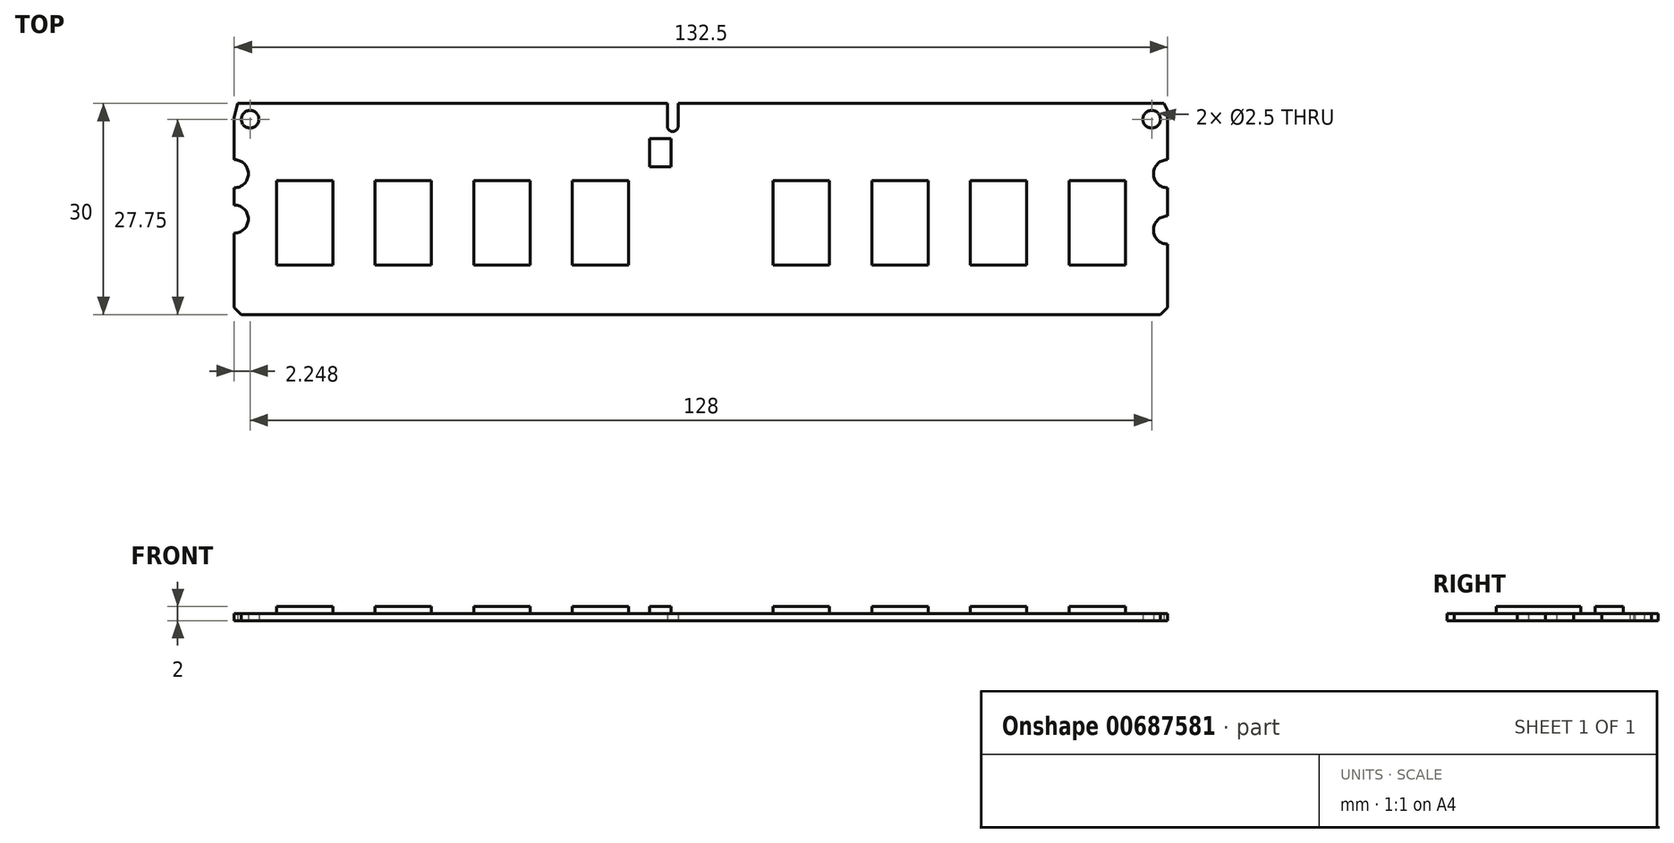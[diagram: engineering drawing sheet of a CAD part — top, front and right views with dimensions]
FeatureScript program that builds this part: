
annotation { "Feature Type Name" : "Feature", "Feature Type Description" : "" }
export const myFeature = defineFeature(function(context is Context, id is Id, definition is map)
    precondition{}
    {
        {
            var Q0;
            Q0=qCreatedBy(makeId("Top.planeOp"),FACE);
            var sketch = newSketch(context, id + "F0", { "sketchPlane" : qUnion([Q0])});
            skLineSegment(sketch, "E0.bottom", {"start": v(-59.31, 12) * mm, "end": v(1.69, 12) * mm});
            skLineSegment(sketch, "E0.top", {"start": v(-58.81, -18) * mm, "end": v(71.69, -18) * mm});
            skLineSegment(sketch, "E0.left", {"start": v(-59.81, 10) * mm, "end": v(-59.81, 4) * mm});
            skLineSegment(sketch, "E0.right", {"start": v(72.69, 11) * mm, "end": v(72.69, 4) * mm});
            skArc(sketch, "E1", {"start": v(72.69, 4) * mm, "mid": v(70.69, 2) * mm, "end": v(72.69, 0) * mm});
            skLineSegment(sketch, "E2", {"start": v(72.69, -17) * mm, "end": v(72.69, -8) * mm});
            skArc(sketch, "E3", {"start": v(72.69, -4) * mm, "mid": v(70.69, -6) * mm, "end": v(72.69, -8) * mm});
            skLineSegment(sketch, "E4.trimOffspring", {"start": v(72.69, -8) * mm, "end": v(72.69, -17) * mm});
            skLineSegment(sketch, "E5.trimOffspring", {"start": v(72.69, 0) * mm, "end": v(72.69, -4) * mm});
            skLineSegment(sketch, "E6", {"start": v(-59.81, -17) * mm, "end": v(-59.81, -6.44) * mm});
            skArc(sketch, "E7", {"start": v(-59.81, 0) * mm, "mid": v(-57.81, 2) * mm, "end": v(-59.81, 4) * mm});
            skArc(sketch, "E8", {"start": v(-59.81, -6.44) * mm, "mid": v(-57.81, -4.44) * mm, "end": v(-59.81, -2.44) * mm});
            skLineSegment(sketch, "E9.trimOffspring", {"start": v(-59.81, -6.44) * mm, "end": v(-59.81, -17) * mm});
            skLineSegment(sketch, "E10.trimOffspring", {"start": v(-59.81, 0) * mm, "end": v(-59.81, -2.44) * mm});
            skLineSegment(sketch, "E11", {"start": v(-59.81, 10) * mm, "end": v(-59.31, 12) * mm});
            skPoint(sketch, "E12.orphan", {"position": v(-59.81, 12) * mm});
            skPoint(sketch, "E13.start.orphan", {"position": v(73.14, 10.06) * mm});
            skLineSegment(sketch, "E14", {"start": v(72.19, 12) * mm, "end": v(72.69, 11) * mm});
            skPoint(sketch, "E15.orphan", {"position": v(72.69, 12) * mm});
            skLineSegment(sketch, "E16", {"start": v(72.69, -17) * mm, "end": v(71.69, -18) * mm});
            skPoint(sketch, "E17.orphan", {"position": v(72.69, -18) * mm});
            skLineSegment(sketch, "E18", {"start": v(-59.81, -17) * mm, "end": v(-58.81, -18) * mm});
            skPoint(sketch, "E19.orphan", {"position": v(-59.81, -18) * mm});
            skLineSegment(sketch, "E20", {"start": v(1.69, 12) * mm, "end": v(1.69, 8.65) * mm});
            skPoint(sketch, "E21.end.orphan", {"position": v(3.19, 12) * mm});
            skLineSegment(sketch, "E22", {"start": v(3.19, 12) * mm, "end": v(3.19, 8.65) * mm});
            skArc(sketch, "E23", {"start": v(1.69, 8.65) * mm, "mid": v(2.44, 8) * mm, "end": v(3.19, 8.65) * mm});
            skPoint(sketch, "E24.orphan", {"position": v(1.69, 8) * mm});
            skLineSegment(sketch, "E25.trimOffspring", {"start": v(3.19, 12) * mm, "end": v(72.19, 12) * mm});
            skPoint(sketch, "E26.end.orphan", {"position": v(3.19, 8) * mm});
            skPoint(sketch, "E26.start.orphan", {"position": v(2.44, 8) * mm});
            skCircle(sketch, "E27", {"center": v(70.44, 9.75) * mm, "radius": 1.25 * mm});
            skPoint(sketch, "E28.end.orphan", {"position": v(70.44, 11) * mm});
            skPoint(sketch, "E29.end.orphan", {"position": v(71.69, 9.75) * mm});
            skCircle(sketch, "E30", {"center": v(-57.56, 9.75) * mm, "radius": 1.25 * mm});
            skPoint(sketch, "E31.end.orphan", {"position": v(-57.56, 11) * mm});
            skPoint(sketch, "E32.end.orphan", {"position": v(-58.81, 9.75) * mm});
            skSolve(sketch);
        }
        {
            var Q0;
            Q0 = qSketchRegion(id + "F0", true);
            extrude(context, id + "F1", {"entities" : qUnion([Q0]), "depth" : 1 * mm, "offsetDistance" : 25 * mm});
        }
        {
            var Q0;
            Q0=makeQuery(id+"F1.opExtrude","CAP_FACE",FACE,{"disambiguationData":[OSD([sQuery(id+"F0.wireOp",EDGE,"E0.bottom"),sQuery(id+"F0.wireOp",EDGE,"E0.top"),sQuery(id+"F0.wireOp",EDGE,"E0.right"),sQuery(id+"F0.wireOp",EDGE,"E1"),sQuery(id+"F0.wireOp",EDGE,"E3"),sQuery(id+"F0.wireOp",EDGE,"E4.trimOffspring"),sQuery(id+"F0.wireOp",EDGE,"E5.trimOffspring"),sQuery(id+"F0.wireOp",EDGE,"E0.left"),sQuery(id+"F0.wireOp",EDGE,"E7"),sQuery(id+"F0.wireOp",EDGE,"E8"),sQuery(id+"F0.wireOp",EDGE,"E9.trimOffspring"),sQuery(id+"F0.wireOp",EDGE,"E10.trimOffspring"),sQuery(id+"F0.wireOp",EDGE,"E11"),sQuery(id+"F0.wireOp",EDGE,"E14"),sQuery(id+"F0.wireOp",EDGE,"E16"),sQuery(id+"F0.wireOp",EDGE,"E18"),sQuery(id+"F0.wireOp",EDGE,"E20"),sQuery(id+"F0.wireOp",EDGE,"E22"),sQuery(id+"F0.wireOp",EDGE,"E23"),sQuery(id+"F0.wireOp",EDGE,"E25.trimOffspring"),sQuery(id+"F0.wireOp",EDGE,"E27"),sQuery(id+"F0.wireOp",EDGE,"E30")])],"isStart":false});
            var sketch = newSketch(context, id + "F2", { "sketchPlane" : qUnion([Q0])});
            skLineSegment(sketch, "E33.bottom", {"start": v(-53.81, 1) * mm, "end": v(-45.81, 1) * mm});
            skLineSegment(sketch, "E33.top", {"start": v(-53.81, -11) * mm, "end": v(-45.81, -11) * mm});
            skLineSegment(sketch, "E33.left", {"start": v(-53.81, 1) * mm, "end": v(-53.81, -11) * mm});
            skLineSegment(sketch, "E33.right", {"start": v(-45.81, 1) * mm, "end": v(-45.81, -11) * mm});
            skLineSegment(sketch, "E34.bottom", {"start": v(-39.81, 1) * mm, "end": v(-31.81, 1) * mm});
            skLineSegment(sketch, "E34.top", {"start": v(-39.81, -11) * mm, "end": v(-31.81, -11) * mm});
            skLineSegment(sketch, "E34.left", {"start": v(-39.81, 1) * mm, "end": v(-39.81, -11) * mm});
            skLineSegment(sketch, "E34.right", {"start": v(-31.81, 1) * mm, "end": v(-31.81, -11) * mm});
            skLineSegment(sketch, "E35.bottom", {"start": v(-25.81, 1) * mm, "end": v(-17.81, 1) * mm});
            skLineSegment(sketch, "E35.top", {"start": v(-25.81, -11) * mm, "end": v(-17.81, -11) * mm});
            skLineSegment(sketch, "E35.left", {"start": v(-25.81, 1) * mm, "end": v(-25.81, -11) * mm});
            skLineSegment(sketch, "E35.right", {"start": v(-17.81, 1) * mm, "end": v(-17.81, -11) * mm});
            skLineSegment(sketch, "E36.bottom", {"start": v(-11.81, 1) * mm, "end": v(-3.81, 1) * mm});
            skLineSegment(sketch, "E36.top", {"start": v(-11.81, -11) * mm, "end": v(-3.81, -11) * mm});
            skLineSegment(sketch, "E36.left", {"start": v(-11.81, 1) * mm, "end": v(-11.81, -11) * mm});
            skLineSegment(sketch, "E36.right", {"start": v(-3.81, 1) * mm, "end": v(-3.81, -11) * mm});
            skLineSegment(sketch, "E37.bottom", {"start": v(66.69, 1) * mm, "end": v(58.69, 1) * mm});
            skLineSegment(sketch, "E37.top", {"start": v(66.69, -11) * mm, "end": v(58.69, -11) * mm});
            skLineSegment(sketch, "E37.left", {"start": v(66.69, 1) * mm, "end": v(66.69, -11) * mm});
            skLineSegment(sketch, "E37.right", {"start": v(58.69, 1) * mm, "end": v(58.69, -11) * mm});
            skLineSegment(sketch, "E38.bottom", {"start": v(52.69, 1) * mm, "end": v(44.69, 1) * mm});
            skLineSegment(sketch, "E38.top", {"start": v(52.69, -11) * mm, "end": v(44.69, -11) * mm});
            skLineSegment(sketch, "E38.left", {"start": v(52.69, 1) * mm, "end": v(52.69, -11) * mm});
            skLineSegment(sketch, "E38.right", {"start": v(44.69, 1) * mm, "end": v(44.69, -11) * mm});
            skLineSegment(sketch, "E39.bottom", {"start": v(38.69, 1) * mm, "end": v(30.69, 1) * mm});
            skLineSegment(sketch, "E39.top", {"start": v(38.69, -11) * mm, "end": v(30.69, -11) * mm});
            skLineSegment(sketch, "E39.left", {"start": v(38.69, 1) * mm, "end": v(38.69, -11) * mm});
            skLineSegment(sketch, "E39.right", {"start": v(30.69, 1) * mm, "end": v(30.69, -11) * mm});
            skLineSegment(sketch, "E40.bottom", {"start": v(24.69, 1) * mm, "end": v(16.69, 1) * mm});
            skLineSegment(sketch, "E40.top", {"start": v(24.69, -11) * mm, "end": v(16.69, -11) * mm});
            skLineSegment(sketch, "E40.left", {"start": v(24.69, 1) * mm, "end": v(24.69, -11) * mm});
            skLineSegment(sketch, "E40.right", {"start": v(16.69, 1) * mm, "end": v(16.69, -11) * mm});
            skLineSegment(sketch, "E41.bottom", {"start": v(-0.81, 7) * mm, "end": v(2.19, 7) * mm});
            skLineSegment(sketch, "E41.top", {"start": v(-0.81, 3) * mm, "end": v(2.19, 3) * mm});
            skLineSegment(sketch, "E41.left", {"start": v(-0.81, 7) * mm, "end": v(-0.81, 3) * mm});
            skLineSegment(sketch, "E41.right", {"start": v(2.19, 7) * mm, "end": v(2.19, 3) * mm});
            skSolve(sketch);
        }
        {
            var Q0;
            Q0 = qSketchRegion(id + "F2", true);
            extrude(context, id + "F3", {"entities" : qUnion([Q0]), "operationType" : NewBodyOperationType.ADD, "depth" : 1 * mm, "offsetDistance" : 25 * mm});
        }
    });
